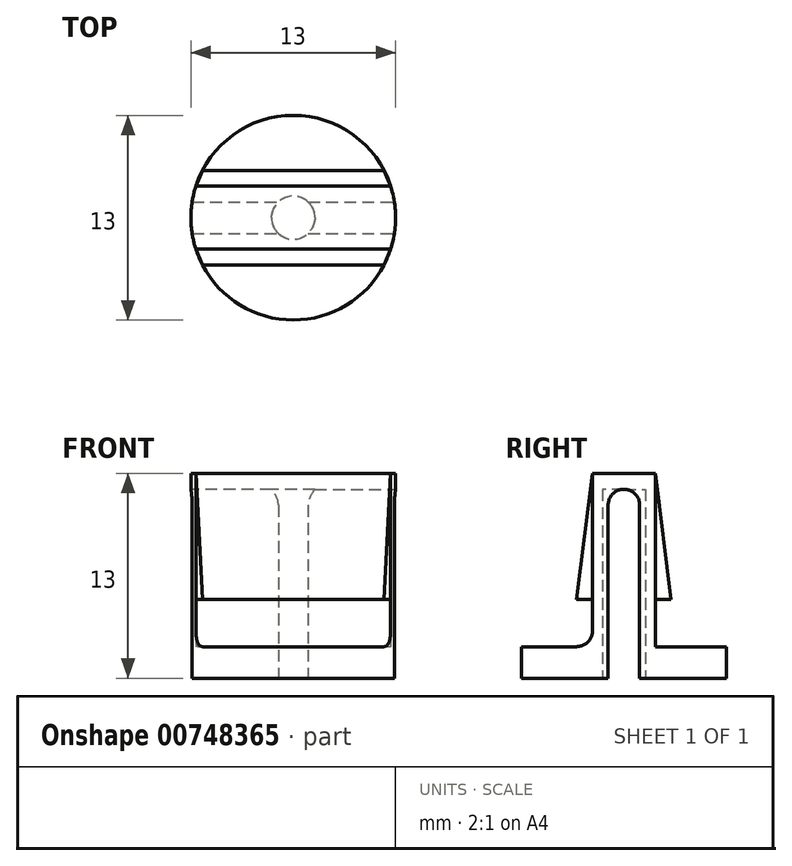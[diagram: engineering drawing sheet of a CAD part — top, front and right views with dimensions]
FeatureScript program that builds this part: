
annotation { "Feature Type Name" : "Feature", "Feature Type Description" : "" }
export const myFeature = defineFeature(function(context is Context, id is Id, definition is map)
    precondition{}
    {
        {
            var Q0;
            Q0=qCreatedBy(makeId("Top.planeOp"),FACE);
            var sketch = newSketch(context, id + "F0", { "sketchPlane" : qUnion([Q0])});
            skCircle(sketch, "E0", {"center": v(0, 0) * mm, "radius": 6.5 * mm});
            skSolve(sketch);
        }
        {
            var Q0;
            Q0=makeQuery(id+"F0.imprint","IMPRINT",FACE,{"disambiguationData":[TD([[makeQuery(id+"F0.imprint","IMPRINT",EDGE,{"derivedFrom":sQuery(id+"F0.wireOp",EDGE,"E0")}),1.0]])]});
            extrude(context, id + "F1", {"entities" : qUnion([Q0]), "endBound" : BoundingType.SYMMETRIC, "depth" : 2 * mm, "offsetDistance" : 25 * mm});
        }
        {
            var Q0;
            Q0=makeQuery(id+"F1.opExtrude","CAP_FACE",FACE,{"disambiguationData":[OSD([sQuery(id+"F0.wireOp",EDGE,"E0")])],"isStart":false});
            var sketch = newSketch(context, id + "F2", { "sketchPlane" : qUnion([Q0])});
            skLineSegment(sketch, "E1.bottom", {"start": v(6.18, 2) * mm, "end": v(-6.18, 2) * mm});
            skLineSegment(sketch, "E1.top", {"start": v(6.18, -2) * mm, "end": v(-6.18, -2) * mm});
            skPoint(sketch, "E1.middle", {"position": v(0, 0) * mm});
            skArc(sketch, "E2", {"start": v(-6.18, 2) * mm, "mid": v(-6.5, 0) * mm, "end": v(-6.18, -2) * mm});
            skArc(sketch, "E3.trimOffspring", {"start": v(6.18, -2) * mm, "mid": v(6.5, 0) * mm, "end": v(6.18, 2) * mm});
            skSolve(sketch);
        }
        {
            var Q0;
            Q0=makeQuery(id+"F2.imprint","IMPRINT",FACE,{"disambiguationData":[TD([[makeQuery(id+"F2.imprint","IMPRINT",EDGE,{"derivedFrom":sQuery(id+"F2.wireOp",EDGE,"E1.bottom")}),1.0]])]});
            extrude(context, id + "F3", {"entities" : qUnion([Q0]), "operationType" : NewBodyOperationType.ADD, "depth" : 11 * mm, "offsetDistance" : 25 * mm});
        }
        {
            var Q0;
            {var subQ0=sQuery(id+"F0.wireOp",EDGE,"E0");Q0=makeQuery(id+"F3.boolean.opBoolean","SPLIT",FACE,{"disambiguationData":[TD([makeQuery(id+"F3.opExtrude","SWEPT_FACE",FACE,{"disambiguationData":[OSD([sQuery(id+"F2.wireOp",EDGE,"E1.bottom")])]})])],"derivedFrom":makeQuery(id+"F1.opExtrude","CAP_FACE",FACE,{"disambiguationData":[OSD([subQ0])],"isStart":false})});}
            cPlane(context, id + "F4", {"entities" : qUnion([Q0]), "cplaneType" : CPlaneType.OFFSET, "offset" : 3 * mm, "width" : 150 * mm, "height" : 150 * mm});
        }
        {
            var Q0;
            Q0=qCreatedBy(id+"F4.planeOp",FACE);
            var sketch = newSketch(context, id + "F5", { "sketchPlane" : qUnion([Q0])});
            skLineSegment(sketch, "E4.bottom", {"start": v(5.77, 3) * mm, "end": v(-5.77, 3) * mm});
            skLineSegment(sketch, "E4.top", {"start": v(5.77, -3) * mm, "end": v(-5.77, -3) * mm});
            skPoint(sketch, "E4.middle", {"position": v(0, 0) * mm});
            skArc(sketch, "E5", {"start": v(-5.77, 3) * mm, "mid": v(-6.5, 0) * mm, "end": v(-5.77, -3) * mm});
            skArc(sketch, "E6.trimOffspring", {"start": v(5.77, -3) * mm, "mid": v(6.5, 0) * mm, "end": v(5.77, 3) * mm});
            skSolve(sketch);
        }
        {
            var Q1;
            Q1=makeQuery(id+"F5.imprint","IMPRINT",FACE,{"disambiguationData":[TD([[makeQuery(id+"F5.imprint","IMPRINT",EDGE,{"derivedFrom":sQuery(id+"F5.wireOp",EDGE,"E4.bottom")}),1.0]])]});
            var Q2;
            Q2=makeQuery(id+"F3.opExtrude","CAP_FACE",FACE,{"disambiguationData":[OSD([sQuery(id+"F2.wireOp",EDGE,"E1.bottom"),sQuery(id+"F2.wireOp",EDGE,"E1.top"),sQuery(id+"F2.wireOp",EDGE,"E2"),sQuery(id+"F2.wireOp",EDGE,"E3.trimOffspring")])],"isStart":false});
            loft(context, id + "F6", {"operationType" : NewBodyOperationType.ADD, "sheetProfilesArray" : [{ "sheetProfileEntities" : qUnion([Q1]) }, { "sheetProfileEntities" : qUnion([Q2]) }]});
        }
        {
            var Q0;
            Q0=makeQuery(id+"F1.opExtrude","CAP_FACE",FACE,{"disambiguationData":[OSD([sQuery(id+"F0.wireOp",EDGE,"E0")])],"isStart":true});
            var sketch = newSketch(context, id + "F7", { "sketchPlane" : qUnion([Q0])});
            skCircle(sketch, "E7", {"center": v(0, 0) * mm, "radius": 1.38 * mm});
            skSolve(sketch);
        }
        {
            var Q0;
            Q0 = qSketchRegion(id + "F7", true);
            extrude(context, id + "F8", {"entities" : qUnion([Q0]), "operationType" : NewBodyOperationType.REMOVE, "oppositeDirection" : true, "depth" : 12 * mm, "offsetDistance" : 25 * mm});
        }
        {
            var Q0;
            Q0=makeQuery(id+"F1.opExtrude","CAP_FACE",FACE,{"disambiguationData":[OSD([sQuery(id+"F0.wireOp",EDGE,"E0")])],"isStart":true});
            var sketch = newSketch(context, id + "F9", { "sketchPlane" : qUnion([Q0])});
            skLineSegment(sketch, "E8.bottom", {"start": v(-23.24, -1) * mm, "end": v(23.24, -1) * mm});
            skLineSegment(sketch, "E8.top", {"start": v(-23.24, 1) * mm, "end": v(23.24, 1) * mm});
            skLineSegment(sketch, "E8.left", {"start": v(-23.24, -1) * mm, "end": v(-23.24, 1) * mm});
            skLineSegment(sketch, "E8.right", {"start": v(23.24, -1) * mm, "end": v(23.24, 1) * mm});
            skPoint(sketch, "E8.middle", {"position": v(0, 0) * mm});
            skSolve(sketch);
        }
        {
            var Q0;
            Q0 = qSketchRegion(id + "F9", true);
            extrude(context, id + "F10", {"entities" : qUnion([Q0]), "operationType" : NewBodyOperationType.REMOVE, "oppositeDirection" : true, "depth" : 12 * mm, "offsetDistance" : 25 * mm});
        }
        {
            var Q0;
            Q0=makeQuery(id+"F10.boolean.opBoolean","COPY",EDGE,{"disambiguationData":[OD(1.0)],"derivedFrom":makeQuery(id+"F10.opExtrude","CAP_EDGE",EDGE,{"disambiguationData":[OSD([sQuery(id+"F9.wireOp",EDGE,"E8.bottom")])],"isStart":false})});
            var Q1;
            Q1=makeQuery(id+"F10.boolean.opBoolean","COPY",EDGE,{"disambiguationData":[OD(1.0)],"derivedFrom":makeQuery(id+"F10.opExtrude","CAP_EDGE",EDGE,{"disambiguationData":[OSD([sQuery(id+"F9.wireOp",EDGE,"E8.top")])],"isStart":false})});
            var Q2;
            Q2=makeQuery(id+"F10.boolean.opBoolean","COPY",EDGE,{"disambiguationData":[OD(0.0)],"derivedFrom":makeQuery(id+"F10.opExtrude","CAP_EDGE",EDGE,{"disambiguationData":[OSD([sQuery(id+"F9.wireOp",EDGE,"E8.top")])],"isStart":false})});
            var Q3;
            Q3=makeQuery(id+"F10.boolean.opBoolean","COPY",EDGE,{"disambiguationData":[OD(0.0)],"derivedFrom":makeQuery(id+"F10.opExtrude","CAP_EDGE",EDGE,{"disambiguationData":[OSD([sQuery(id+"F9.wireOp",EDGE,"E8.bottom")])],"isStart":false})});
            var Q4;
            Q4=makeQuery(id+"F3.opExtrude","CAP_EDGE",EDGE,{"disambiguationData":[OSD([sQuery(id+"F2.wireOp",EDGE,"E1.bottom")])],"isStart":true});
            var Q5;
            Q5=makeQuery(id+"F3.opExtrude","CAP_EDGE",EDGE,{"disambiguationData":[OSD([sQuery(id+"F2.wireOp",EDGE,"E1.top")])],"isStart":true});
            fillet(context, id + "F11", {"entities" : qUnion([Q0, Q1, Q2, Q3, Q4, Q5]), "radius" : 1 * mm, "tangentPropagation" : true, "allowEdgeOverflow" : false});
        }
    });
